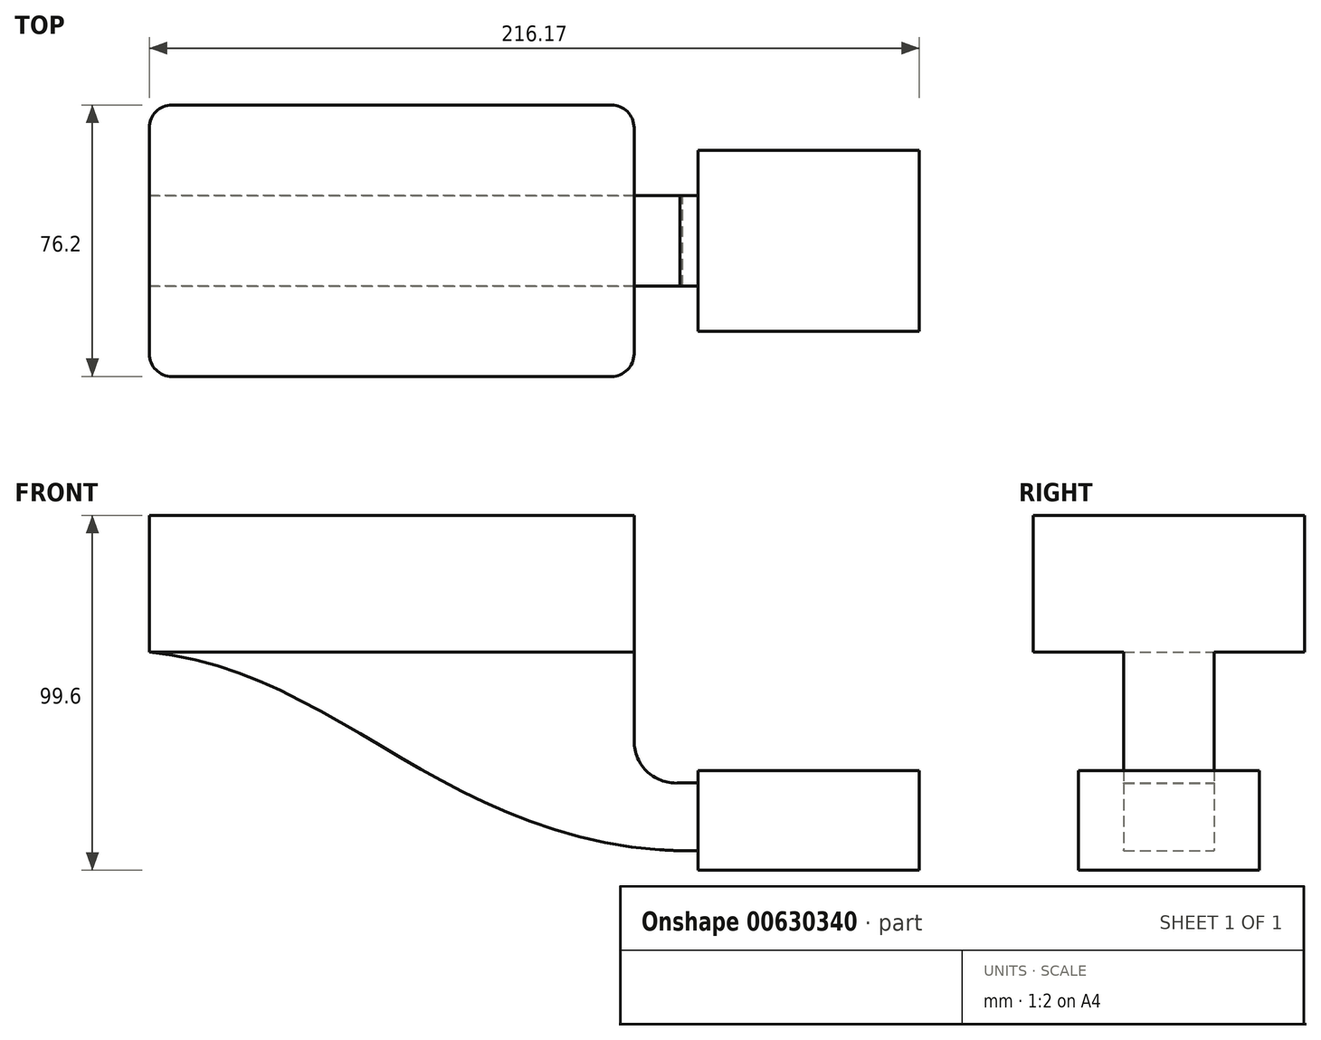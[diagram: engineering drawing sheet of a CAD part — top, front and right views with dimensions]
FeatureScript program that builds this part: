
annotation { "Feature Type Name" : "Feature", "Feature Type Description" : "" }
export const myFeature = defineFeature(function(context is Context, id is Id, definition is map)
    precondition{}
    {
        {
            var Q0;
            Q0=qCreatedBy(makeId("Front.planeOp"),FACE);
            var sketch = newSketch(context, id + "F0", { "sketchPlane" : qUnion([Q0])});
            skLineSegment(sketch, "E0.bottom", {"start": v(68.04, -19.2) * mm, "end": v(-68.04, -19.2) * mm});
            skLineSegment(sketch, "E0.top", {"start": v(68.04, 19.2) * mm, "end": v(-68.04, 19.2) * mm});
            skLineSegment(sketch, "E0.left", {"start": v(68.04, -19.2) * mm, "end": v(68.04, 19.2) * mm});
            skLineSegment(sketch, "E0.right", {"start": v(-68.04, -19.2) * mm, "end": v(-68.04, 19.2) * mm});
            skPoint(sketch, "E0.middle", {"position": v(0, 0) * mm});
            skLineSegment(sketch, "E1.bottom", {"start": v(85.95, -52.4) * mm, "end": v(148.13, -52.4) * mm});
            skLineSegment(sketch, "E1.top", {"start": v(85.95, -80.4) * mm, "end": v(148.13, -80.4) * mm});
            skLineSegment(sketch, "E1.left", {"start": v(85.95, -52.4) * mm, "end": v(85.95, -80.4) * mm});
            skLineSegment(sketch, "E1.right", {"start": v(148.13, -52.4) * mm, "end": v(148.13, -80.4) * mm});
            skPoint(sketch, "E1.middle", {"position": v(117.04, -66.4) * mm});
            skLineSegment(sketch, "E2", {"start": v(68.04, -19.2) * mm, "end": v(68.04, -44.16) * mm});
            skArc(sketch, "E3", {"start": v(68.04, -44.16) * mm, "mid": v(71.91, -52.89) * mm, "end": v(80.98, -55.88) * mm});
            skLineSegment(sketch, "E4", {"start": v(80.98, -55.88) * mm, "end": v(108.08, -55.88) * mm});
            skLineSegment(sketch, "E5.0", {"start": v(81.7, -74.93) * mm, "end": v(108.08, -74.93) * mm});
            skArc(sketch, "E5.1", {"start": v(49, -44.16) * mm, "mid": v(58.7, -66.61) * mm, "end": v(81.7, -74.93) * mm});
            skLineSegment(sketch, "E5.2", {"start": v(49, -19.2) * mm, "end": v(49, -44.16) * mm});
            skLineSegment(sketch, "E6", {"start": v(108.08, -52.4) * mm, "end": v(108.08, -80.4) * mm});
            skFitSpline(sketch, "E7", {"points": [v(-68.04, -19.2) * mm, v(81.7, -74.93) * mm], "startDerivative": vector(158.11, -14.35) * mm, "endDerivative": vector(197.83, -3.99) * mm});
            skSolve(sketch);
        }
        {
            var Q0;
            Q0=makeQuery(id+"F0.imprint","IMPRINT",FACE,{"disambiguationData":[TD([[makeQuery(id+"F0.imprint","IMPRINT",EDGE,{"derivedFrom":sQuery(id+"F0.wireOp",EDGE,"E0.top")}),1.0]])]});
            extrude(context, id + "F1", {"entities" : qUnion([Q0]), "endBound" : BoundingType.SYMMETRIC, "depth" : 76.2 * mm, "offsetDistance" : 25.4 * mm});
        }
        {
            var Q0;
            {var subQ3=sQuery(id+"F0.wireOp",EDGE,"E5.2");Q0=makeQuery(id+"F0.imprint","IMPRINT",FACE,{"disambiguationData":[TD([[makeQuery(id+"F0.imprint","IMPRINT",EDGE,{"derivedFrom":subQ3}),-1.0]])]});}
            var Q1;
            {var subQ1=sQuery(id+"F0.wireOp",EDGE,"E2");Q1=makeQuery(id+"F0.imprint","IMPRINT",FACE,{"disambiguationData":[TD([[makeQuery(id+"F0.imprint","IMPRINT",EDGE,{"derivedFrom":subQ1}),-1.0]])]});}
            extrude(context, id + "F2", {"entities" : qUnion([Q0, Q1]), "operationType" : NewBodyOperationType.ADD, "endBound" : BoundingType.SYMMETRIC, "depth" : 25.4 * mm, "offsetDistance" : 25.4 * mm});
        }
        {
            var Q0;
            {var subQ4=sQuery(id+"F0.wireOp",EDGE,"E1.right");Q0=makeQuery(id+"F0.imprint","IMPRINT",FACE,{"disambiguationData":[TD([[makeQuery(id+"F0.imprint","IMPRINT",EDGE,{"derivedFrom":subQ4}),-1.0]])]});}
            var Q1;
            {var subQ0=sQuery(id+"F0.wireOp",EDGE,"E4");var subQ1=sQuery(id+"F0.wireOp",EDGE,"E1.left");var subQ2=makeQuery(id+"F0.imprint","INTERSECT",VERTEX,{"derivedFrom":[subQ1,subQ0]});Q1=makeQuery(id+"F0.imprint","IMPRINT",FACE,{"disambiguationData":[TD([[makeQuery(id+"F0.imprint","IMPRINT",EDGE,{"disambiguationData":[TD([[subQ2,-1.0]])],"derivedFrom":subQ1}),1.0]])]});}
            var Q2;
            {var subQ0=sQuery(id+"F0.wireOp",EDGE,"E1.left");var subQ1=sQuery(id+"F0.wireOp",EDGE,"E1.top");var subQ2=makeQuery(id+"F0.imprint","INTERSECT",VERTEX,{"derivedFrom":[subQ1,subQ0]});Q2=makeQuery(id+"F0.imprint","IMPRINT",FACE,{"disambiguationData":[TD([[makeQuery(id+"F0.imprint","IMPRINT",EDGE,{"disambiguationData":[TD([[subQ2,-1.0]])],"derivedFrom":subQ1}),1.0]])]});}
            var Q3;
            {var subQ0=sQuery(id+"F0.wireOp",EDGE,"E1.left");var subQ1=sQuery(id+"F0.wireOp",EDGE,"E1.bottom");var subQ2=makeQuery(id+"F0.imprint","INTERSECT",VERTEX,{"derivedFrom":[subQ1,subQ0]});Q3=makeQuery(id+"F0.imprint","IMPRINT",FACE,{"disambiguationData":[TD([[makeQuery(id+"F0.imprint","IMPRINT",EDGE,{"disambiguationData":[TD([[subQ2,-1.0]])],"derivedFrom":subQ1}),-1.0]])]});}
            extrude(context, id + "F3", {"entities" : qUnion([Q0, Q1, Q2, Q3]), "operationType" : NewBodyOperationType.ADD, "endBound" : BoundingType.SYMMETRIC, "depth" : 50.8 * mm, "offsetDistance" : 25.4 * mm});
        }
        {
            var Q0;
            Q0=makeQuery(id+"F1.opExtrude","CAP_EDGE",EDGE,{"disambiguationData":[OSD([sQuery(id+"F0.wireOp",EDGE,"E0.left")])],"isStart":false});
            var Q1;
            Q1=makeQuery(id+"F1.opExtrude","CAP_EDGE",EDGE,{"disambiguationData":[OSD([sQuery(id+"F0.wireOp",EDGE,"E0.right")])],"isStart":false});
            var Q2;
            Q2=makeQuery(id+"F1.opExtrude","CAP_EDGE",EDGE,{"disambiguationData":[OSD([sQuery(id+"F0.wireOp",EDGE,"E0.right")])],"isStart":true});
            var Q3;
            Q3=makeQuery(id+"F1.opExtrude","CAP_EDGE",EDGE,{"disambiguationData":[OSD([sQuery(id+"F0.wireOp",EDGE,"E0.left")])],"isStart":true});
            fillet(context, id + "F4", {"entities" : qUnion([Q0, Q1, Q2, Q3]), "radius" : 6.35 * mm, "tangentPropagation" : true, "allowEdgeOverflow" : false});
        }
    });
